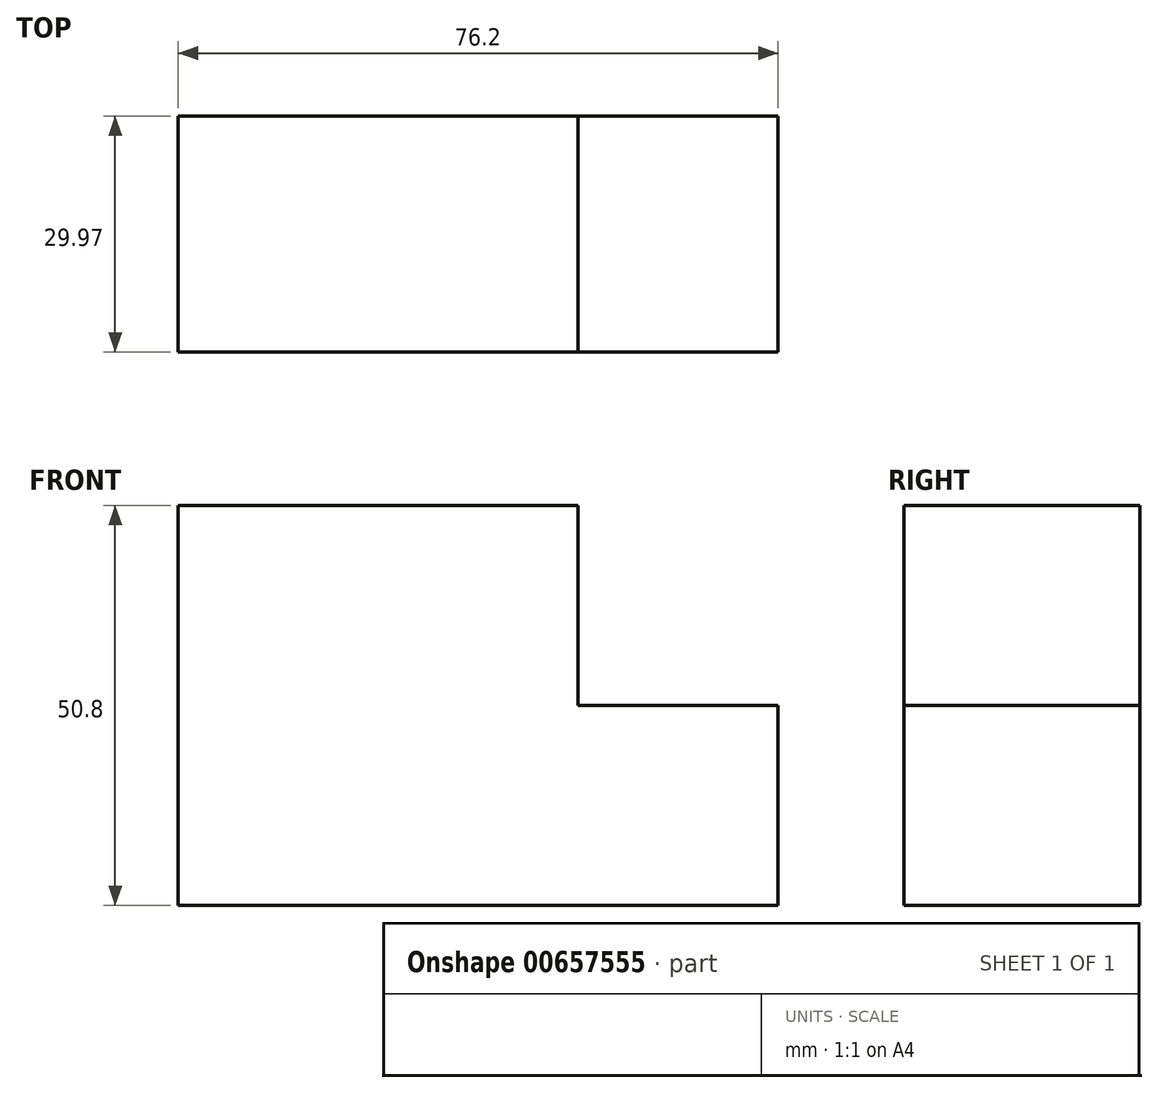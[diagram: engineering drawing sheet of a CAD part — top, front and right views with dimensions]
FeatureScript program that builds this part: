
annotation { "Feature Type Name" : "Feature", "Feature Type Description" : "" }
export const myFeature = defineFeature(function(context is Context, id is Id, definition is map)
    precondition{}
    {
        {
            var Q0;
            Q0=qCreatedBy(makeId("Front.planeOp"),FACE);
            var sketch = newSketch(context, id + "F0", { "sketchPlane" : qUnion([Q0])});
            skLineSegment(sketch, "E0", {"start": v(-39.85, -33.34) * mm, "end": v(36.35, -33.34) * mm});
            skLineSegment(sketch, "E1", {"start": v(36.35, -33.34) * mm, "end": v(36.35, -7.94) * mm});
            skLineSegment(sketch, "E2", {"start": v(36.35, -7.94) * mm, "end": v(10.95, -7.94) * mm});
            skLineSegment(sketch, "E3", {"start": v(10.95, -7.94) * mm, "end": v(10.95, 17.46) * mm});
            skLineSegment(sketch, "E4", {"start": v(10.95, 17.46) * mm, "end": v(-39.85, 17.46) * mm});
            skLineSegment(sketch, "E5", {"start": v(-39.85, 17.46) * mm, "end": v(-39.85, -33.34) * mm});
            skSolve(sketch);
        }
        {
            var Q0;
            Q0=makeQuery(id+"F0.imprint","IMPRINT",FACE,{"disambiguationData":[TD([[makeQuery(id+"F0.imprint","IMPRINT",EDGE,{"derivedFrom":sQuery(id+"F0.wireOp",EDGE,"E0")}),1.0]])]});
            extrude(context, id + "F1", {"entities" : qUnion([Q0]), "depth" : 29.97 * mm, "offsetDistance" : 25.4 * mm});
        }
    });
